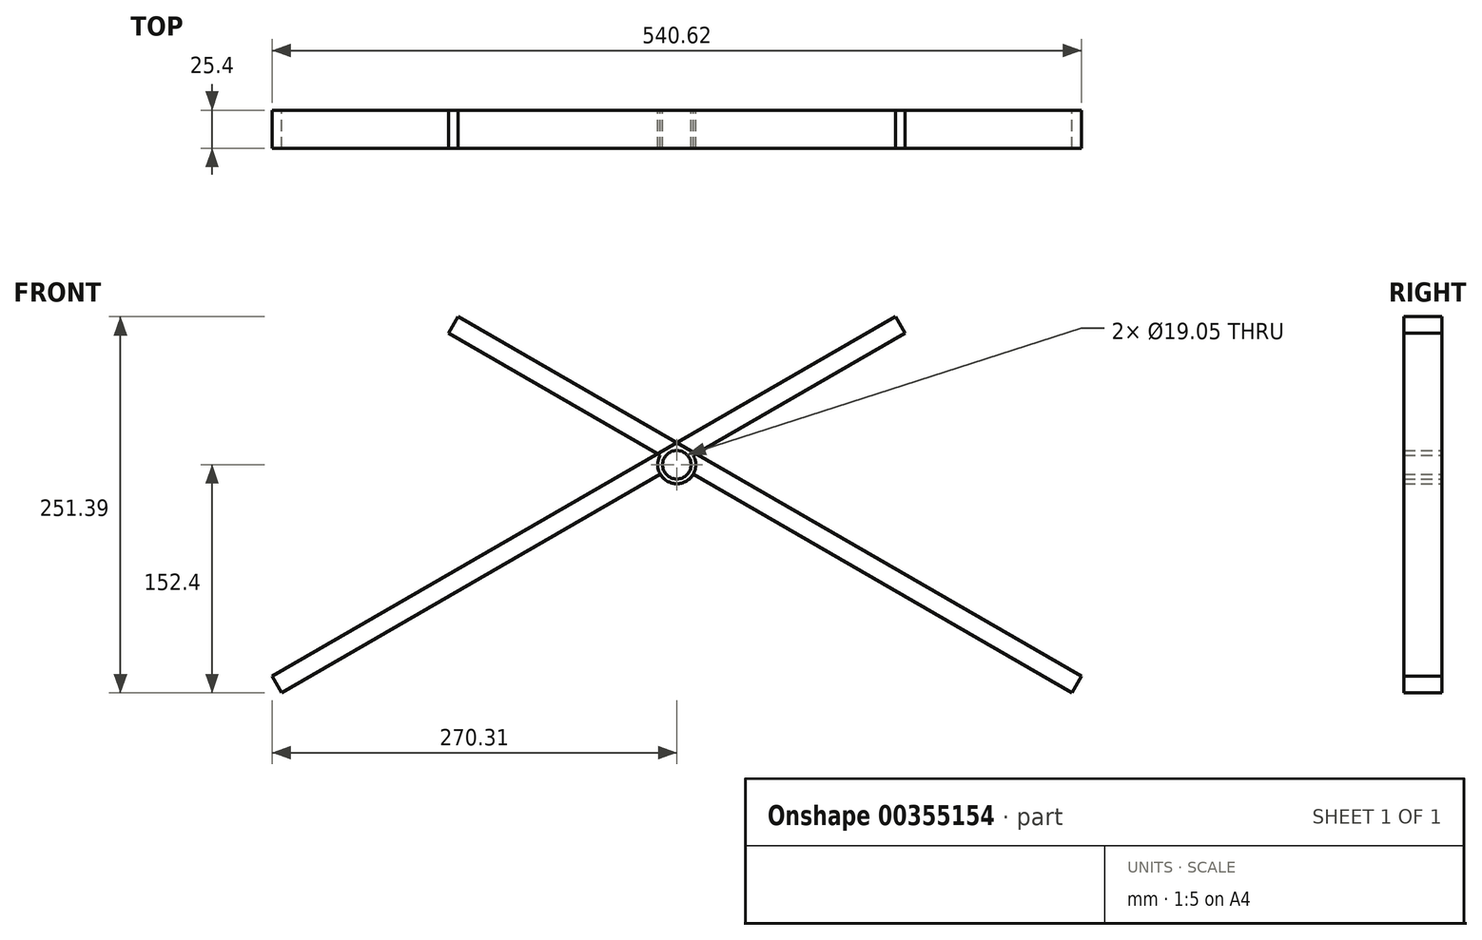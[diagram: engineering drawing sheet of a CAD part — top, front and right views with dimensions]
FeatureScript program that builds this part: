
annotation { "Feature Type Name" : "Feature", "Feature Type Description" : "" }
export const myFeature = defineFeature(function(context is Context, id is Id, definition is map)
    precondition{}
    {
        {
            var Q0;
            Q0=qCreatedBy(makeId("Front.planeOp"),FACE);
            var sketch = newSketch(context, id + "F0", { "sketchPlane" : qUnion([Q0])});
            skLineSegment(sketch, "E0", {"start": v(-87.99, -152.4) * mm, "end": v(263.96, -152.4) * mm, "construction": true});
            skLineSegment(sketch, "E1", {"start": v(263.96, -152.4) * mm, "end": v(0, 0) * mm});
            skLineSegment(sketch, "E2", {"start": v(0, 0) * mm, "end": v(-87.99, -152.4) * mm, "construction": true});
            skLineSegment(sketch, "E3", {"start": v(0, 0) * mm, "end": v(-152.4, 87.99) * mm});
            skCircle(sketch, "E4", {"center": v(0, 0) * mm, "radius": 12.7 * mm});
            skCircle(sketch, "E5", {"center": v(0, 0) * mm, "radius": 9.53 * mm});
            skLineSegment(sketch, "E6", {"start": v(0, 0) * mm, "end": v(6.35, 11) * mm, "construction": true});
            skLineSegment(sketch, "E7", {"start": v(-152.4, 87.99) * mm, "end": v(-146.05, 98.99) * mm});
            skLineSegment(sketch, "E8", {"start": v(-146.05, 98.99) * mm, "end": v(6.35, 11) * mm});
            skLineSegment(sketch, "E9", {"start": v(6.35, 11) * mm, "end": v(270.31, -141.4) * mm});
            skLineSegment(sketch, "E10", {"start": v(270.31, -141.4) * mm, "end": v(263.96, -152.4) * mm});
            skSolve(sketch);
        }
        {
            var Q0;
            {var subQ0=sQuery(id+"F0.wireOp",EDGE,"E7");Q0=makeQuery(id+"F0.imprint","IMPRINT",FACE,{"disambiguationData":[TD([[makeQuery(id+"F0.imprint","IMPRINT",EDGE,{"derivedFrom":subQ0}),-1.0]])]});}
            var Q1;
            {var subQ0=sQuery(id+"F0.wireOp",EDGE,"E4");var subQ2=sQuery(id+"F0.wireOp",EDGE,"E1");var subQ3=makeQuery(id+"F0.imprint","INTERSECT",VERTEX,{"derivedFrom":[subQ2,subQ0]});Q1=makeQuery(id+"F0.imprint","IMPRINT",FACE,{"disambiguationData":[TD([[makeQuery(id+"F0.imprint","IMPRINT",EDGE,{"disambiguationData":[TD([[subQ3,-1.0]])],"derivedFrom":subQ2}),-1.0]])]});}
            var Q2;
            {var subQ0=sQuery(id+"F0.wireOp",EDGE,"E4");var subQ1=sQuery(id+"F0.wireOp",EDGE,"E1");var subQ2=makeQuery(id+"F0.imprint","INTERSECT",VERTEX,{"derivedFrom":[subQ1,subQ0]});Q2=makeQuery(id+"F0.imprint","IMPRINT",FACE,{"disambiguationData":[TD([[makeQuery(id+"F0.imprint","IMPRINT",EDGE,{"disambiguationData":[TD([[subQ2,-1.0]])],"derivedFrom":subQ1}),1.0]])]});}
            var Q3;
            {var subQ4=sQuery(id+"F0.wireOp",EDGE,"E9");Q3=makeQuery(id+"F0.imprint","IMPRINT",FACE,{"disambiguationData":[TD([[makeQuery(id+"F0.imprint","IMPRINT",EDGE,{"derivedFrom":subQ4}),-1.0]])]});}
            extrude(context, id + "F1", {"entities" : qUnion([Q0, Q1, Q2, Q3]), "endBound" : BoundingType.SYMMETRIC, "depth" : 25.4 * mm});
        }
        {
            var Q0;
            Q0=makeQuery(id+"F1.opExtrude","SWEPT_BODY",BODY,{"disambiguationData":[OSD([sQuery(id+"F0.wireOp",EDGE,"E1"),sQuery(id+"F0.wireOp",EDGE,"E3"),sQuery(id+"F0.wireOp",EDGE,"E4"),sQuery(id+"F0.wireOp",EDGE,"E5"),sQuery(id+"F0.wireOp",EDGE,"E7"),sQuery(id+"F0.wireOp",EDGE,"E8"),sQuery(id+"F0.wireOp",EDGE,"E9"),sQuery(id+"F0.wireOp",EDGE,"E10")])]});
            var Q1;
            Q1=qCreatedBy(makeId("Right.planeOp"),FACE);
            mirror(context, id + "F2", {"entities" : qUnion([Q0]), "mirrorPlane" : qUnion([Q1])});
        }
    });
